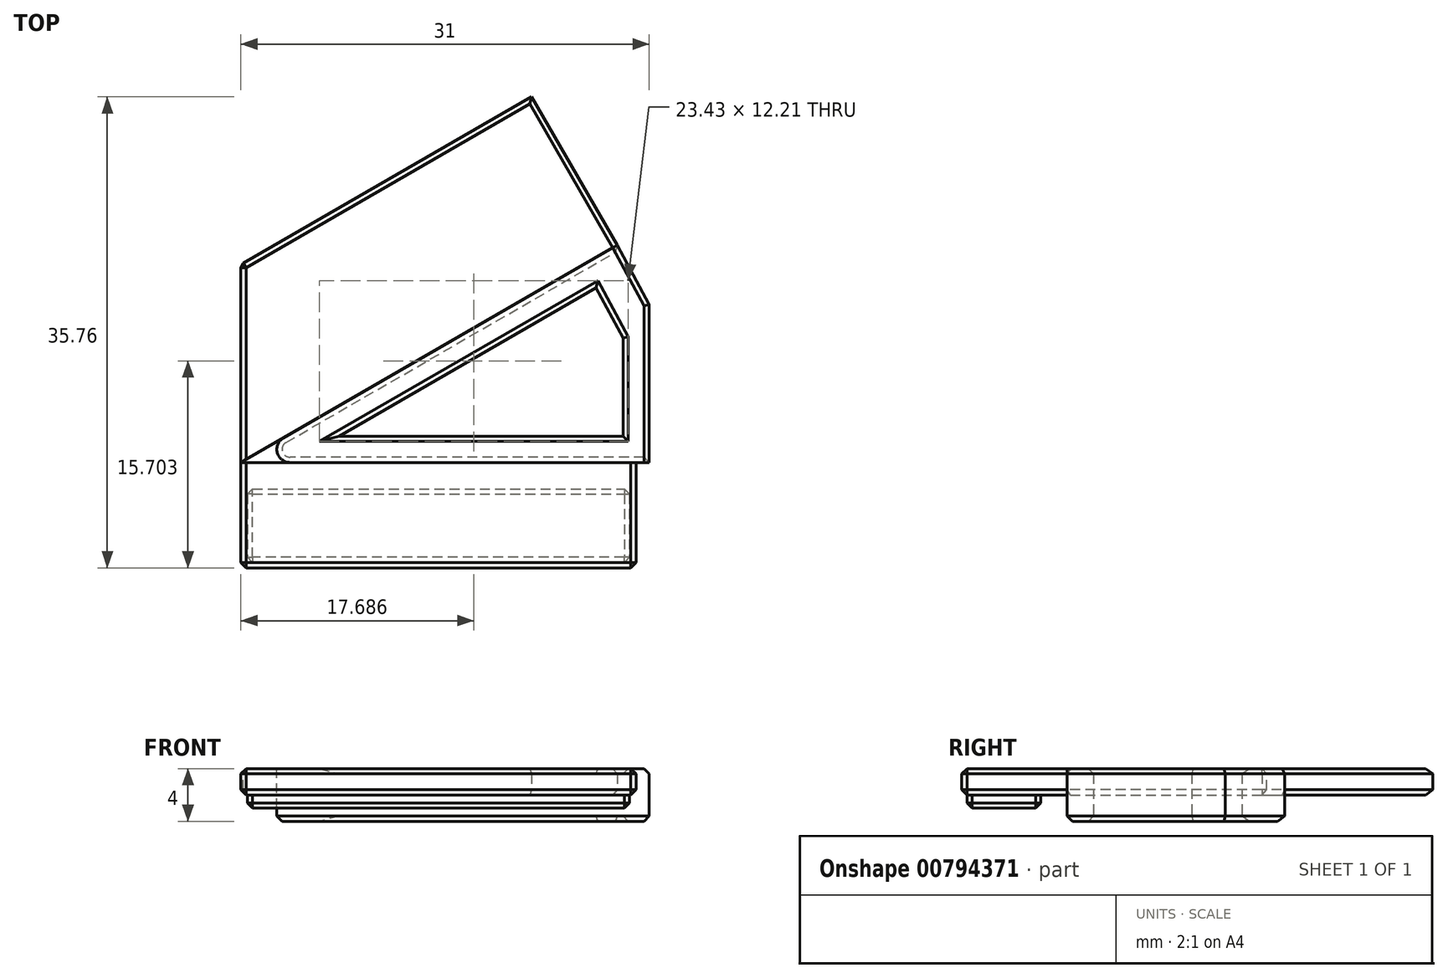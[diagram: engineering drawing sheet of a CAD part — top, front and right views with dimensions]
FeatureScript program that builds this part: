
annotation { "Feature Type Name" : "Feature", "Feature Type Description" : "" }
export const myFeature = defineFeature(function(context is Context, id is Id, definition is map)
    precondition{}
    {
        {
            var Q0;
            Q0=qCreatedBy(makeId("Top.planeOp"),FACE);
            var sketch = newSketch(context, id + "F0", { "sketchPlane" : qUnion([Q0])});
            skLineSegment(sketch, "E0", {"start": v(0, 0) * mm, "end": v(31, 0) * mm});
            skLineSegment(sketch, "E1", {"start": v(0, 0) * mm, "end": v(28.58, 16.5) * mm});
            skLineSegment(sketch, "E2", {"start": v(31, 0) * mm, "end": v(31, 12) * mm});
            skLineSegment(sketch, "E3", {"start": v(31, 12) * mm, "end": v(28.58, 16.5) * mm});
            skLineSegment(sketch, "E4", {"start": v(7.46, 2) * mm, "end": v(29, 2) * mm});
            skLineSegment(sketch, "E5", {"start": v(7.46, 2) * mm, "end": v(26.96, 13.25) * mm});
            skLineSegment(sketch, "E6", {"start": v(29, 2) * mm, "end": v(29, 9.45) * mm});
            skLineSegment(sketch, "E7", {"start": v(26.96, 13.25) * mm, "end": v(29, 9.45) * mm});
            skSolve(sketch);
        }
        {
            var Q0;
            Q0=makeQuery(id+"F0.imprint","IMPRINT",FACE,{"disambiguationData":[TD([[makeQuery(id+"F0.imprint","IMPRINT",EDGE,{"derivedFrom":sQuery(id+"F0.wireOp",EDGE,"E0")}),1.0]])]});
            extrude(context, id + "F1", {"entities" : qUnion([Q0]), "endBound" : BoundingType.SYMMETRIC, "depth" : 4 * mm, "offsetDistance" : 25 * mm});
        }
        {
            var Q0;
            Q0=qCreatedBy(makeId("Top.planeOp"),FACE);
            var sketch = newSketch(context, id + "F2", { "sketchPlane" : qUnion([Q0])});
            skLineSegment(sketch, "E8.bottom", {"start": v(0, 0) * mm, "end": v(30, 0) * mm});
            skLineSegment(sketch, "E8.top", {"start": v(0, -8) * mm, "end": v(30, -8) * mm});
            skLineSegment(sketch, "E8.left", {"start": v(0, 0) * mm, "end": v(0, -8) * mm});
            skLineSegment(sketch, "E8.right", {"start": v(30, 0) * mm, "end": v(30, -8) * mm});
            skLineSegment(sketch, "E9", {"start": v(0, 0) * mm, "end": v(28.58, 16.5) * mm});
            skLineSegment(sketch, "E10", {"start": v(28.58, 16.5) * mm, "end": v(22.08, 27.76) * mm});
            skLineSegment(sketch, "E11", {"start": v(22.08, 27.76) * mm, "end": v(0, 15.01) * mm});
            skLineSegment(sketch, "E12.MirrorCS", {"start": v(0, 15.01) * mm, "end": v(0, 0) * mm});
            skLineSegment(sketch, "E13.bottom", {"start": v(0.5, -2) * mm, "end": v(29.5, -2) * mm});
            skLineSegment(sketch, "E13.top", {"start": v(0.5, -7.6) * mm, "end": v(29.5, -7.6) * mm});
            skLineSegment(sketch, "E13.left", {"start": v(0.5, -2) * mm, "end": v(0.5, -7.6) * mm});
            skLineSegment(sketch, "E13.right", {"start": v(29.5, -2) * mm, "end": v(29.5, -7.6) * mm});
            skSolve(sketch);
        }
        {
            var Q0;
            Q0=makeQuery(id+"F2.imprint","IMPRINT",FACE,{"disambiguationData":[TD([[makeQuery(id+"F2.imprint","IMPRINT",EDGE,{"derivedFrom":sQuery(id+"F2.wireOp",EDGE,"E8.bottom")}),-1.0]])]});
            var Q1;
            {var subQ1=sQuery(id+"F2.wireOp",EDGE,"E9");Q1=makeQuery(id+"F2.imprint","IMPRINT",FACE,{"disambiguationData":[TD([[makeQuery(id+"F2.imprint","IMPRINT",EDGE,{"derivedFrom":subQ1}),1.0]])]});}
            extrude(context, id + "F3", {"entities" : qUnion([Q0, Q1]), "depth" : 2 * mm, "offsetDistance" : 25 * mm});
        }
        {
            var Q0;
            Q0=makeQuery(id+"F1.opExtrude","SWEPT_EDGE",EDGE,{"disambiguationData":[OSD([sQuery(id+"F0.wireOp",EDGE,"E0"),sQuery(id+"F0.wireOp",EDGE,"E1")])]});
            fillet(context, id + "F4", {"entities" : qUnion([Q0]), "radius" : 1 * mm, "tangentPropagation" : true, "allowEdgeOverflow" : false});
        }
        {
            var Q0;
            Q0=makeQuery(id+"F2.imprint","IMPRINT",FACE,{"disambiguationData":[TD([[makeQuery(id+"F2.imprint","IMPRINT",EDGE,{"derivedFrom":sQuery(id+"F2.wireOp",EDGE,"E13.bottom")}),-1.0]])]});
            extrude(context, id + "F5", {"entities" : qUnion([Q0]), "operationType" : NewBodyOperationType.ADD, "oppositeDirection" : true, "depth" : 1 * mm, "offsetDistance" : 25 * mm, "hasSecondDirection" : true, "secondDirectionOppositeDirection" : false, "secondDirectionDepth" : 2 * mm});
        }
        {
            var Q0;
            Q0=makeQuery(id+"F3.opExtrude","CAP_EDGE",EDGE,{"disambiguationData":[OSD([sQuery(id+"F2.wireOp",EDGE,"E11")])],"isStart":true});
            var Q1;
            Q1=makeQuery(id+"F3.opExtrude","CAP_EDGE",EDGE,{"disambiguationData":[OSD([sQuery(id+"F2.wireOp",EDGE,"E11")])],"isStart":false});
            var Q2;
            Q2=makeQuery(id+"F3.opExtrude","SWEPT_EDGE",EDGE,{"disambiguationData":[OSD([sQuery(id+"F2.wireOp",EDGE,"E11"),sQuery(id+"F2.wireOp",EDGE,"E12.MirrorCS")])]});
            var Q3;
            Q3=makeQuery(id+"F3.opExtrude","CAP_EDGE",EDGE,{"disambiguationData":[OSD([sQuery(id+"F2.wireOp",EDGE,"E12.MirrorCS")])],"isStart":true});
            var Q4;
            Q4=makeQuery(id+"F3.opExtrude","CAP_EDGE",EDGE,{"disambiguationData":[OSD([sQuery(id+"F2.wireOp",EDGE,"E12.MirrorCS")])],"isStart":false});
            var Q5;
            Q5=makeQuery(id+"F5.opExtrude","CAP_EDGE",EDGE,{"disambiguationData":[OSD([sQuery(id+"F2.wireOp",EDGE,"E13.left")])],"isStart":false});
            var Q6;
            Q6=makeQuery(id+"F5.opExtrude","CAP_EDGE",EDGE,{"disambiguationData":[OSD([sQuery(id+"F2.wireOp",EDGE,"E13.bottom")])],"isStart":false});
            var Q7;
            Q7=makeQuery(id+"F5.opExtrude","CAP_EDGE",EDGE,{"disambiguationData":[OSD([sQuery(id+"F2.wireOp",EDGE,"E13.right")])],"isStart":false});
            var Q8;
            Q8=makeQuery(id+"F5.opExtrude","CAP_EDGE",EDGE,{"disambiguationData":[OSD([sQuery(id+"F2.wireOp",EDGE,"E13.top")])],"isStart":false});
            var Q9;
            Q9=makeQuery(id+"F3.opExtrude","CAP_EDGE",EDGE,{"disambiguationData":[OSD([sQuery(id+"F2.wireOp",EDGE,"E8.left")])],"isStart":false});
            var Q10;
            Q10=makeQuery(id+"F3.opExtrude","SWEPT_EDGE",EDGE,{"disambiguationData":[OSD([sQuery(id+"F2.wireOp",EDGE,"E8.top"),sQuery(id+"F2.wireOp",EDGE,"E8.left")])]});
            var Q11;
            Q11=makeQuery(id+"F3.opExtrude","CAP_EDGE",EDGE,{"disambiguationData":[OSD([sQuery(id+"F2.wireOp",EDGE,"E10")])],"isStart":true});
            var Q12;
            Q12=makeQuery(id+"F3.opExtrude","CAP_EDGE",EDGE,{"disambiguationData":[OSD([sQuery(id+"F2.wireOp",EDGE,"E10")])],"isStart":false});
            var Q13;
            Q13=makeQuery(id+"F1.opExtrude","CAP_EDGE",EDGE,{"disambiguationData":[OSD([sQuery(id+"F0.wireOp",EDGE,"E3")])],"isStart":true});
            var Q14;
            Q14=makeQuery(id+"F1.opExtrude","CAP_EDGE",EDGE,{"disambiguationData":[OSD([sQuery(id+"F0.wireOp",EDGE,"E2")])],"isStart":true});
            var Q15;
            Q15=makeQuery(id+"F3.opExtrude","CAP_EDGE",EDGE,{"disambiguationData":[OSD([sQuery(id+"F2.wireOp",EDGE,"E8.right")])],"isStart":false});
            var Q16;
            Q16=makeQuery(id+"F3.opExtrude","SWEPT_EDGE",EDGE,{"disambiguationData":[OSD([sQuery(id+"F2.wireOp",EDGE,"E8.top"),sQuery(id+"F2.wireOp",EDGE,"E8.right")])]});
            var Q17;
            Q17=makeQuery(id+"F3.opExtrude","CAP_EDGE",EDGE,{"disambiguationData":[OSD([sQuery(id+"F2.wireOp",EDGE,"E8.top")])],"isStart":false});
            var Q18;
            Q18=makeQuery(id+"F1.opExtrude","CAP_EDGE",EDGE,{"disambiguationData":[OSD([sQuery(id+"F0.wireOp",EDGE,"E5")])],"isStart":false});
            var Q19;
            Q19=makeQuery(id+"F1.opExtrude","CAP_EDGE",EDGE,{"disambiguationData":[OSD([sQuery(id+"F0.wireOp",EDGE,"E4")])],"isStart":false});
            var Q20;
            Q20=makeQuery(id+"F1.opExtrude","CAP_EDGE",EDGE,{"disambiguationData":[OSD([sQuery(id+"F0.wireOp",EDGE,"E6")])],"isStart":false});
            var Q21;
            Q21=makeQuery(id+"F1.opExtrude","CAP_EDGE",EDGE,{"disambiguationData":[OSD([sQuery(id+"F0.wireOp",EDGE,"E7")])],"isStart":false});
            var Q22;
            Q22=makeQuery(id+"F1.opExtrude","CAP_EDGE",EDGE,{"disambiguationData":[OSD([sQuery(id+"F0.wireOp",EDGE,"E4")])],"isStart":true});
            var Q23;
            Q23=makeQuery(id+"F1.opExtrude","CAP_EDGE",EDGE,{"disambiguationData":[OSD([sQuery(id+"F0.wireOp",EDGE,"E6")])],"isStart":true});
            var Q24;
            Q24=makeQuery(id+"F1.opExtrude","CAP_EDGE",EDGE,{"disambiguationData":[OSD([sQuery(id+"F0.wireOp",EDGE,"E7")])],"isStart":true});
            var Q25;
            Q25=makeQuery(id+"F1.opExtrude","CAP_EDGE",EDGE,{"disambiguationData":[OSD([sQuery(id+"F0.wireOp",EDGE,"E5")])],"isStart":true});
            var Q26;
            Q26=makeQuery(id+"F5.opExtrude","SWEPT_EDGE",EDGE,{"disambiguationData":[OSD([sQuery(id+"F2.wireOp",EDGE,"E13.bottom"),sQuery(id+"F2.wireOp",EDGE,"E13.left")])]});
            var Q27;
            Q27=makeQuery(id+"F5.opExtrude","SWEPT_EDGE",EDGE,{"disambiguationData":[OSD([sQuery(id+"F2.wireOp",EDGE,"E13.top"),sQuery(id+"F2.wireOp",EDGE,"E13.left")])]});
            var Q28;
            Q28=makeQuery(id+"F5.opExtrude","SWEPT_EDGE",EDGE,{"disambiguationData":[OSD([sQuery(id+"F2.wireOp",EDGE,"E13.top"),sQuery(id+"F2.wireOp",EDGE,"E13.right")])]});
            var Q29;
            Q29=makeQuery(id+"F5.opExtrude","SWEPT_EDGE",EDGE,{"disambiguationData":[OSD([sQuery(id+"F2.wireOp",EDGE,"E13.bottom"),sQuery(id+"F2.wireOp",EDGE,"E13.right")])]});
            var Q30;
            Q30=makeQuery(id+"F1.opExtrude","CAP_EDGE",EDGE,{"disambiguationData":[OSD([sQuery(id+"F0.wireOp",EDGE,"E1")])],"isStart":true});
            var Q31;
            Q31=makeQuery(id+"F1.opExtrude","CAP_EDGE",EDGE,{"disambiguationData":[OSD([sQuery(id+"F0.wireOp",EDGE,"E3")])],"isStart":false});
            var Q32;
            Q32=makeQuery(id+"F1.opExtrude","CAP_EDGE",EDGE,{"disambiguationData":[OSD([sQuery(id+"F0.wireOp",EDGE,"E2")])],"isStart":false});
            var Q33;
            Q33=makeQuery(id+"F3.opExtrude","CAP_EDGE",EDGE,{"disambiguationData":[OSD([sQuery(id+"F2.wireOp",EDGE,"E8.left")])],"isStart":true});
            var Q34;
            Q34=makeQuery(id+"F3.opExtrude","CAP_EDGE",EDGE,{"disambiguationData":[OSD([sQuery(id+"F2.wireOp",EDGE,"E8.top")])],"isStart":true});
            var Q35;
            Q35=makeQuery(id+"F3.opExtrude","CAP_EDGE",EDGE,{"disambiguationData":[OSD([sQuery(id+"F2.wireOp",EDGE,"E8.right")])],"isStart":true});
            chamfer(context, id + "F6", {"entities" : qUnion([Q0, Q1, Q2, Q3, Q4, Q5, Q6, Q7, Q8, Q9, Q10, Q11, Q12, Q13, Q14, Q15, Q16, Q17, Q18, Q19, Q20, Q21, Q22, Q23, Q24, Q25, Q26, Q27, Q28, Q29, Q30, Q31, Q32, Q33, Q34, Q35]), "width" : .4 * mm, "tangentPropagation" : true});
        }
    });
